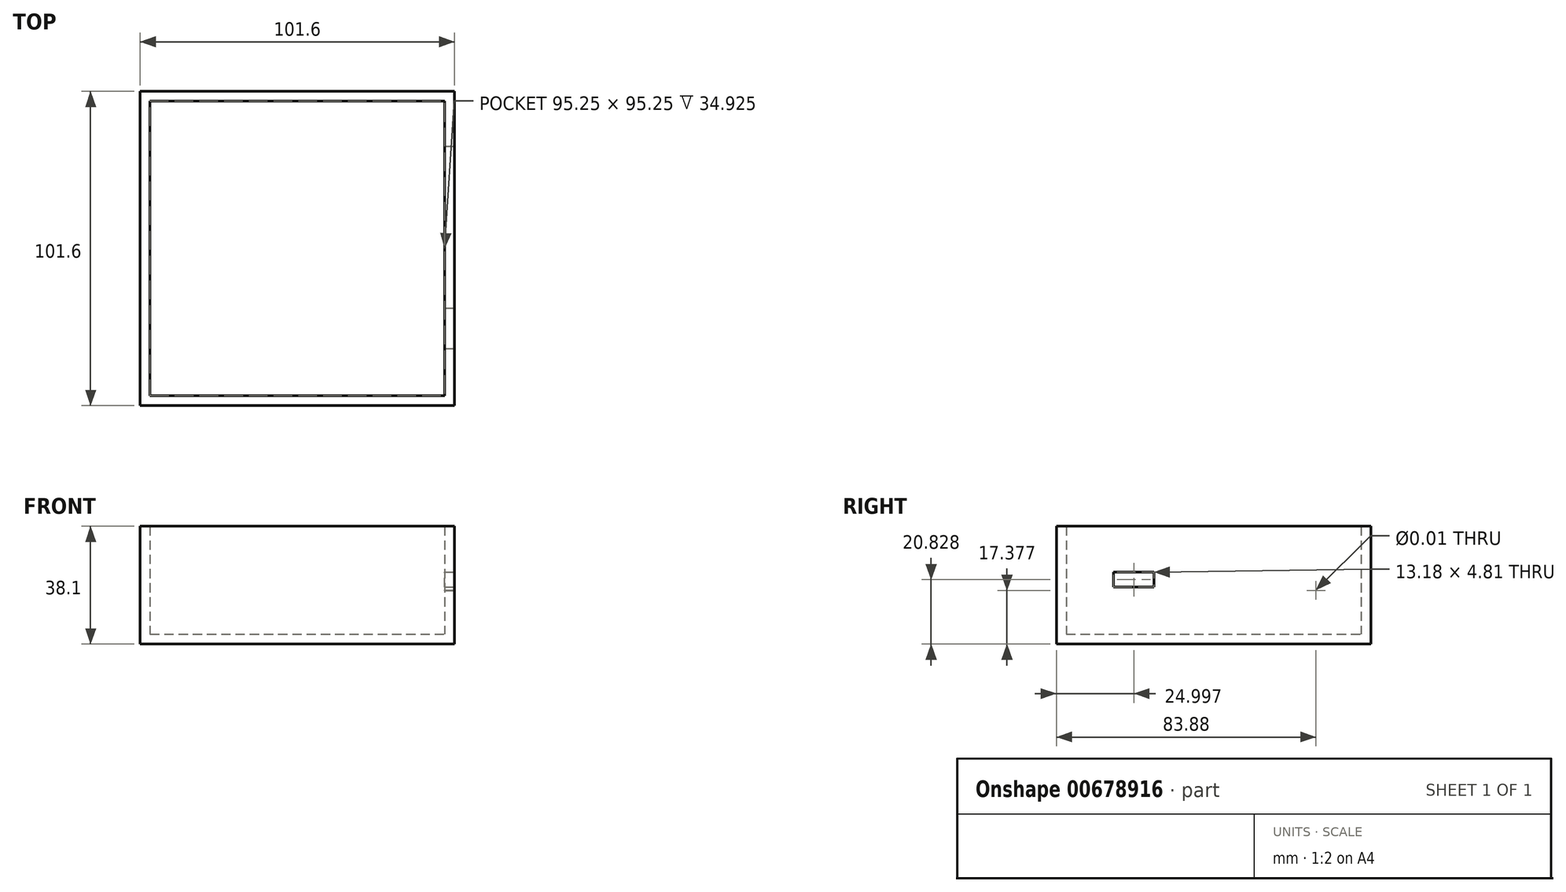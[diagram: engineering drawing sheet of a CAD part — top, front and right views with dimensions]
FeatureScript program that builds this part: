
annotation { "Feature Type Name" : "Feature", "Feature Type Description" : "" }
export const myFeature = defineFeature(function(context is Context, id is Id, definition is map)
    precondition{}
    {
        {
            var Q0;
            Q0=qCreatedBy(makeId("Front.planeOp"),FACE);
            var sketch = newSketch(context, id + "F0", { "sketchPlane" : qUnion([Q0])});
            skLineSegment(sketch, "E0.bottom", {"start": v(-40.76, 26.58) * mm, "end": v(60.84, 26.58) * mm});
            skLineSegment(sketch, "E0.top", {"start": v(-40.76, -11.52) * mm, "end": v(60.84, -11.52) * mm});
            skLineSegment(sketch, "E0.left", {"start": v(-40.76, 26.58) * mm, "end": v(-40.76, -11.52) * mm});
            skLineSegment(sketch, "E0.right", {"start": v(60.84, 26.58) * mm, "end": v(60.84, -11.52) * mm});
            skSolve(sketch);
        }
        {
            var Q0;
            Q0=makeQuery(id+"F0.imprint","IMPRINT",FACE,{"disambiguationData":[TD([[makeQuery(id+"F0.imprint","IMPRINT",EDGE,{"derivedFrom":sQuery(id+"F0.wireOp",EDGE,"E0.bottom")}),-1.0]])]});
            extrude(context, id + "F1", {"entities" : qUnion([Q0]), "depth" : 101.6 * mm, "offsetDistance" : 25.4 * mm});
        }
        {
            var Q0;
            Q0=makeQuery(id+"F1.opExtrude","SWEPT_FACE",FACE,{"disambiguationData":[OSD([sQuery(id+"F0.wireOp",EDGE,"E0.bottom")])]});
            shell(context, id + "F2", {"entities" : qUnion([Q0]), "thickness" : 3.17 * mm});
        }
        {
            var Q0;
            Q0=makeQuery(id+"F1.opExtrude","SWEPT_FACE",FACE,{"disambiguationData":[OSD([sQuery(id+"F0.wireOp",EDGE,"E0.right")])]});
            var sketch = newSketch(context, id + "F3", { "sketchPlane" : qUnion([Q0])});
            skPoint(sketch, "E1", {"position": v(-17.72, 5.86) * mm});
            skLineSegment(sketch, "E2.bottom", {"start": v(-83.2, 11.71) * mm, "end": v(-70.01, 11.71) * mm});
            skLineSegment(sketch, "E2.top", {"start": v(-83.2, 6.9) * mm, "end": v(-70.01, 6.9) * mm});
            skLineSegment(sketch, "E2.left", {"start": v(-83.2, 11.71) * mm, "end": v(-83.2, 6.9) * mm});
            skLineSegment(sketch, "E2.right", {"start": v(-70.01, 11.71) * mm, "end": v(-70.01, 6.9) * mm});
            skSolve(sketch);
        }
        {
            var Q0;
            Q0=sQuery(id+"F3.wireOp",VERTEX,"E1");
            var Q1;
            Q1=makeQuery(id+"F1.opExtrude","SWEPT_BODY",BODY,{"disambiguationData":[OSD([sQuery(id+"F0.wireOp",EDGE,"E0.bottom"),sQuery(id+"F0.wireOp",EDGE,"E0.top"),sQuery(id+"F0.wireOp",EDGE,"E0.left"),sQuery(id+"F0.wireOp",EDGE,"E0.right")])]});
            hole(context, id + "F4", {"style" : HoleStyle.SIMPLE, "endStyle" : HoleEndStyle.BLIND, "holeDiameter" : 5 / 406.4 * mm, "majorDiameter" : 6.35 * mm, "holeDepth" : 12.7 * mm, "isTappedThrough" : true, "tappedDepth" : 12.7 * mm, "tapClearance" : 3, "locations" : qUnion([Q0]), "scope" : qUnion([Q1])});
        }
        {
            var Q0;
            Q0 = qSketchRegion(id + "F3", true);
            extrude(context, id + "F5", {"entities" : qUnion([Q0]), "operationType" : NewBodyOperationType.REMOVE, "endBound" : BoundingType.UP_TO_NEXT, "oppositeDirection" : true, "depth" : 25.4 * mm, "offsetDistance" : 25.4 * mm});
        }
    });
